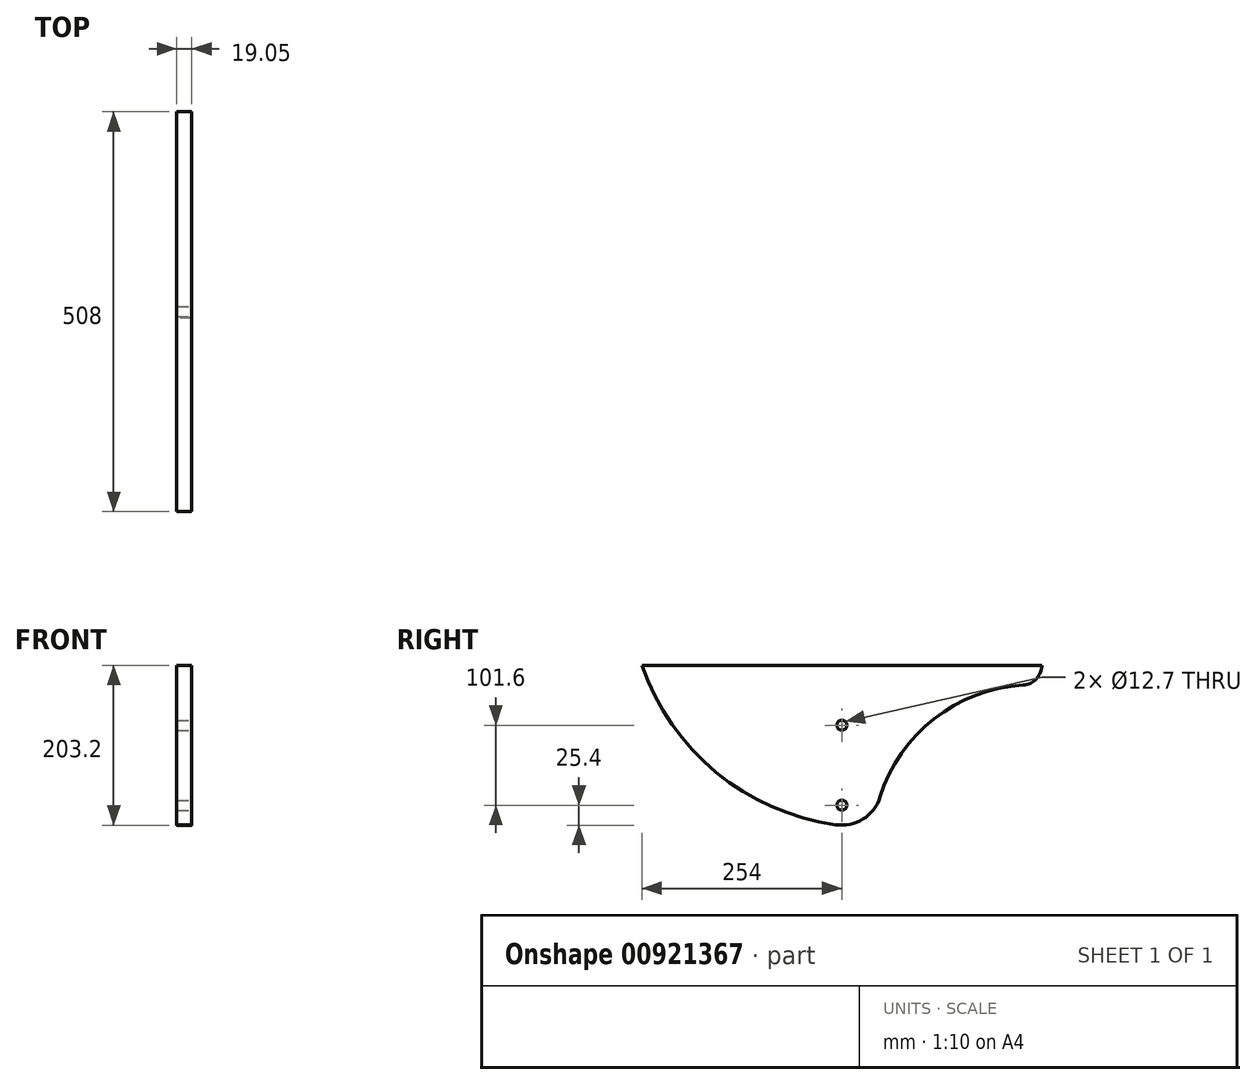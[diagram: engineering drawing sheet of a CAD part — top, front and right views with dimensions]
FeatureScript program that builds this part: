
annotation { "Feature Type Name" : "Feature", "Feature Type Description" : "" }
export const myFeature = defineFeature(function(context is Context, id is Id, definition is map)
    precondition{}
    {
        {
            var Q0;
            Q0=qCreatedBy(makeId("Right.planeOp"),FACE);
            var sketch = newSketch(context, id + "F0", { "sketchPlane" : qUnion([Q0])});
            skLineSegment(sketch, "E0", {"start": v(-254, 0) * mm, "end": v(254, 0) * mm, "construction": true});
            skLineSegment(sketch, "E1", {"start": v(0, 0) * mm, "end": v(0, -203.2) * mm, "construction": true});
            skLineSegment(sketch, "E2", {"start": v(-254, -203.2) * mm, "end": v(254, -203.2) * mm, "construction": true});
            skArc(sketch, "E3", {"start": v(-7.96, -202.57) * mm, "mid": v(26.78, -195.57) * mm, "end": v(48.49, -167.56) * mm});
            skLineSegment(sketch, "E4", {"start": v(-254, 0) * mm, "end": v(-254, -203.2) * mm, "construction": true});
            skLineSegment(sketch, "E5", {"start": v(254, 0) * mm, "end": v(254, -203.2) * mm, "construction": true});
            skPoint(sketch, "E6.first.point", {"position": v(-254, 0) * mm});
            skPoint(sketch, "E6.second.point", {"position": v(-254, -25.4) * mm});
            skPoint(sketch, "E6.third.point", {"position": v(-203.59, -29.8) * mm});
            skPoint(sketch, "E7.first.point", {"position": v(254, 0) * mm});
            skLineSegment(sketch, "E8", {"start": v(-254, 0) * mm, "end": v(254, 0) * mm});
            skArc(sketch, "E9", {"start": v(-254, 0) * mm, "mid": v(-159.56, -136) * mm, "end": v(-7.96, -202.57) * mm});
            skArc(sketch, "E10", {"start": v(230.14, -25.35) * mm, "mid": v(117.18, -68.18) * mm, "end": v(48.49, -167.56) * mm});
            skArc(sketch, "E11", {"start": v(230.14, -25.35) * mm, "mid": v(247.1, -17.4) * mm, "end": v(254, 0) * mm});
            skSolve(sketch);
        }
        {
            var Q0;
            Q0 = qSketchRegion(id + "F0", true);
            extrude(context, id + "F1", {"entities" : qUnion([Q0]), "depth" : 19.05 * mm, "offsetDistance" : 25.4 * mm});
        }
        {
            var Q0;
            Q0=makeQuery(id+"F1.opExtrude","CAP_FACE",FACE,{"disambiguationData":[OSD([sQuery(id+"F0.wireOp",EDGE,"E3"),sQuery(id+"F0.wireOp",EDGE,"E8"),sQuery(id+"F0.wireOp",EDGE,"E9"),sQuery(id+"F0.wireOp",EDGE,"E10"),sQuery(id+"F0.wireOp",EDGE,"E11")])],"isStart":false});
            var sketch = newSketch(context, id + "F2", { "sketchPlane" : qUnion([Q0])});
            skLineSegment(sketch, "E12", {"start": v(0, -205.32) * mm, "end": v(0, 0) * mm, "construction": true});
            skCircle(sketch, "E13", {"center": v(0, -177.8) * mm, "radius": 6.35 * mm});
            skCircle(sketch, "E14", {"center": v(0, -76.2) * mm, "radius": 6.35 * mm});
            skSolve(sketch);
        }
        {
            var Q0;
            Q0 = qSketchRegion(id + "F2", true);
            extrude(context, id + "F3", {"entities" : qUnion([Q0]), "operationType" : NewBodyOperationType.REMOVE, "endBound" : BoundingType.THROUGH_ALL, "oppositeDirection" : true, "depth" : 25.4 * mm, "offsetDistance" : 25.4 * mm});
        }
    });
